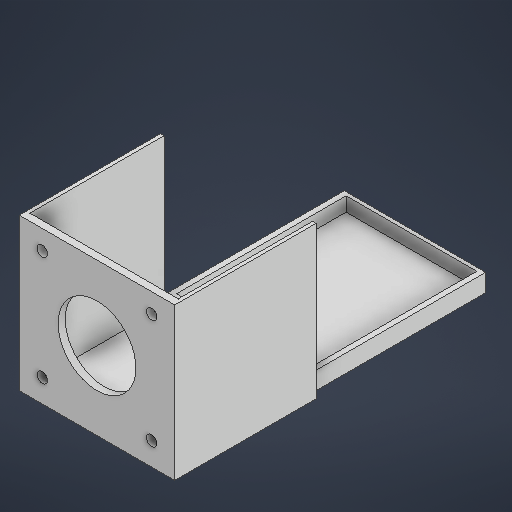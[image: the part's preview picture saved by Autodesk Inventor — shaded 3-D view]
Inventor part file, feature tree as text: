
AUTODESK INVENTOR PART (.ipt)
format: ipt  version: 2025.3 (Build 293356030, 356C)  size: 245,248 bytes
history: native  units: mm
features: sketch x4, extrude x4, projected_geometry x1
ambient origin geometry x8: Origin, YZ Plane, XZ Plane, XY Plane, X Axis, Y Axis, Z Axis, Center Point
bodies: Solid1 (feature_tree)
feature tree (9):
  sketch  "Sketch1"  dims[d0=44.0mm d1=2.95mm]
  extrude  "Extrusion1"  Depth=44.0mm
  extrude  "Extrusion2"  Depth=22.0mm
  extrude  "Extrusion3"  Depth=2.0mm TaperAngle=0.0deg
  extrude  "Extrusion4"  Depth=40.0mm
  sketch  "Sketch Rectangular Pattern1"  dims[d2=20.0mm d4=31.0mm d5=20.0mm d7=31.0mm d10=22.0mm]
  sketch  "Sketch2"  dims[d11=42.0mm d12=2.0mm d13=0.0mm]
  sketch  "Sketch3"  dims[d14=38.0mm d15=0.0mm d16=40.0mm d17=50.0mm d18=0.0mm d19=48.0mm d20=37.0mm d21=4.0mm d22=0.0mm]
  projected_geometry  "Projected Loop1"
